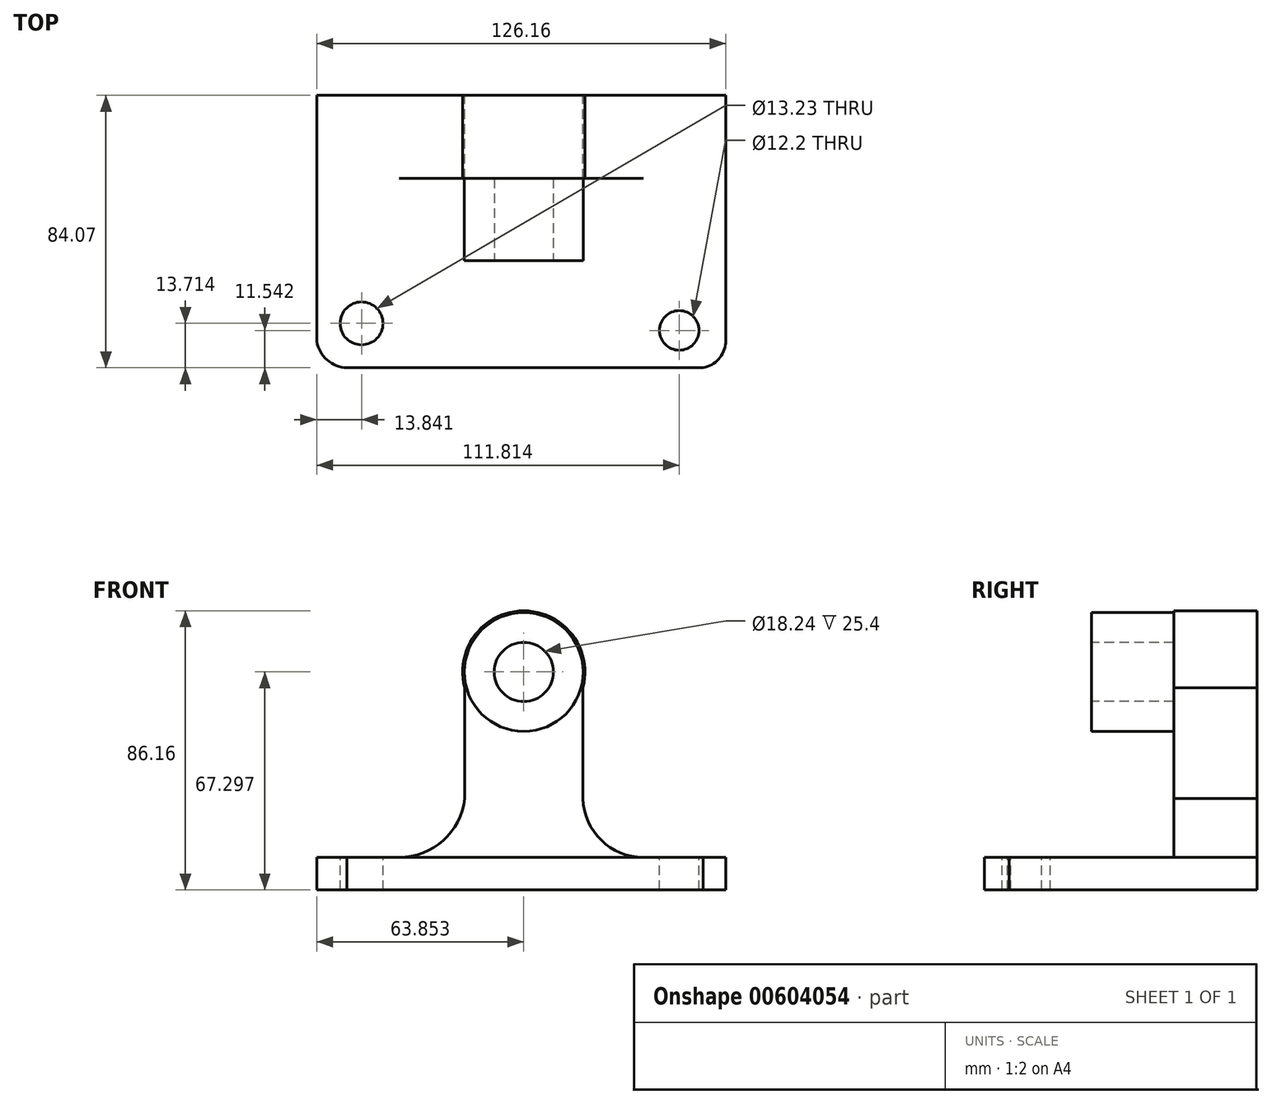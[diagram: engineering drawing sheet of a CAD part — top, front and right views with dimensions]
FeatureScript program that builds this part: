
annotation { "Feature Type Name" : "Feature", "Feature Type Description" : "" }
export const myFeature = defineFeature(function(context is Context, id is Id, definition is map)
    precondition{}
    {
        {
            var Q0;
            Q0=qCreatedBy(makeId("Front.planeOp"),FACE);
            var sketch = newSketch(context, id + "F0", { "sketchPlane" : qUnion([Q0])});
            skLineSegment(sketch, "E0.bottom", {"start": v(-69.62, 0) * mm, "end": v(5.74, 0) * mm});
            skLineSegment(sketch, "E0.top", {"start": v(-69.62, 76.13) * mm, "end": v(5.74, 76.13) * mm});
            skLineSegment(sketch, "E0.left", {"start": v(-69.62, 0) * mm, "end": v(-69.62, 76.13) * mm});
            skLineSegment(sketch, "E0.right", {"start": v(5.74, 0) * mm, "end": v(5.74, 76.13) * mm});
            skSolve(sketch);
        }
        {
            var Q0;
            Q0=makeQuery(id+"F0.imprint","IMPRINT",FACE,{"disambiguationData":[TD([[makeQuery(id+"F0.imprint","IMPRINT",EDGE,{"derivedFrom":sQuery(id+"F0.wireOp",EDGE,"E0.bottom")}),1.0]])]});
            extrude(context, id + "F1", {"entities" : qUnion([Q0]), "depth" : 25.4 * mm, "offsetDistance" : 25.4 * mm});
        }
        {
            var Q0;
            Q0=makeQuery(id+"F1.opExtrude","CAP_FACE",FACE,{"disambiguationData":[OSD([sQuery(id+"F0.wireOp",EDGE,"E0.bottom"),sQuery(id+"F0.wireOp",EDGE,"E0.top"),sQuery(id+"F0.wireOp",EDGE,"E0.left"),sQuery(id+"F0.wireOp",EDGE,"E0.right")])],"isStart":true});
            extrude(context, id + "F2", {"entities" : qUnion([Q0]), "operationType" : NewBodyOperationType.ADD, "depth" : 25.4 * mm, "offsetDistance" : 25.4 * mm});
        }
        {
            var Q0;
            Q0=makeQuery(id+"F2.opExtrude","CAP_FACE",FACE,{"disambiguationData":[OSD([sQuery(id+"F0.wireOp",EDGE,"E0.bottom"),sQuery(id+"F0.wireOp",EDGE,"E0.top"),sQuery(id+"F0.wireOp",EDGE,"E0.left"),sQuery(id+"F0.wireOp",EDGE,"E0.right")])],"isStart":false});
            extrude(context, id + "F3", {"entities" : qUnion([Q0]), "operationType" : NewBodyOperationType.ADD, "depth" : 25.65 * mm, "offsetDistance" : 25.4 * mm});
        }
        {
            var Q0;
            Q0=makeQuery(id+"F3.opExtrude","CAP_FACE",FACE,{"disambiguationData":[OSD([sQuery(id+"F0.wireOp",EDGE,"E0.bottom"),sQuery(id+"F0.wireOp",EDGE,"E0.top"),sQuery(id+"F0.wireOp",EDGE,"E0.left"),sQuery(id+"F0.wireOp",EDGE,"E0.right")])],"isStart":false});
            var sketch = newSketch(context, id + "F4", { "sketchPlane" : qUnion([Q0])});
            skCircle(sketch, "E1", {"center": v(31.17, 57.22) * mm, "radius": 18.86 * mm});
            skSolve(sketch);
        }
        {
            var Q0;
            Q0=makeQuery(id+"F4.imprint","IMPRINT",FACE,{"disambiguationData":[TD([[makeQuery(id+"F4.imprint","IMPRINT",EDGE,{"derivedFrom":sQuery(id+"F4.wireOp",EDGE,"E1")}),-1.0]])]});
            extrude(context, id + "F5", {"entities" : qUnion([Q0]), "operationType" : NewBodyOperationType.REMOVE, "oppositeDirection" : true, "depth" : 25.4 * mm, "offsetDistance" : 25.4 * mm});
        }
        {
            var Q0;
            Q0=makeQuery(id+"F5.boolean.opBoolean","COPY",FACE,{"derivedFrom":makeQuery(id+"F5.opExtrude","CAP_FACE",FACE,{"disambiguationData":[OSD([sQuery(id+"F0.wireOp",EDGE,"E0.bottom"),sQuery(id+"F0.wireOp",EDGE,"E0.top"),sQuery(id+"F0.wireOp",EDGE,"E0.left"),sQuery(id+"F0.wireOp",EDGE,"E0.right"),sQuery(id+"F4.wireOp",EDGE,"E1")])],"isStart":false})});
            var sketch = newSketch(context, id + "F6", { "sketchPlane" : qUnion([Q0])});
            skLineSegment(sketch, "E2", {"start": v(12.94, 62.06) * mm, "end": v(12.94, 18.14) * mm});
            skLineSegment(sketch, "E3", {"start": v(49.4, 62.06) * mm, "end": v(49.4, 18.14) * mm});
            skArc(sketch, "E4", {"start": v(-5.74, 0) * mm, "mid": v(7.28, 5.28) * mm, "end": v(12.94, 18.14) * mm});
            skArc(sketch, "E5", {"start": v(49.4, 18.14) * mm, "mid": v(56.04, 5.2) * mm, "end": v(69.62, 0) * mm});
            skSolve(sketch);
        }
        {
            var Q0;
            {var subQ1=sQuery(id+"F6.wireOp",EDGE,"E4");Q0=makeQuery(id+"F6.imprint","IMPRINT",FACE,{"disambiguationData":[TD([[makeQuery(id+"F6.imprint","IMPRINT",EDGE,{"derivedFrom":subQ1}),1.0]])]});}
            extrude(context, id + "F7", {"entities" : qUnion([Q0]), "operationType" : NewBodyOperationType.REMOVE, "oppositeDirection" : true, "depth" : 25.4 * mm, "offsetDistance" : 25.4 * mm});
        }
        {
            var Q0;
            Q0=makeQuery(id+"F7.boolean.opBoolean","COPY",FACE,{"derivedFrom":makeQuery(id+"F7.opExtrude","CAP_FACE",FACE,{"disambiguationData":[OSD([sQuery(id+"F0.wireOp",EDGE,"E0.top"),sQuery(id+"F0.wireOp",EDGE,"E0.left"),sQuery(id+"F0.wireOp",EDGE,"E0.right"),sQuery(id+"F4.wireOp",EDGE,"E1"),sQuery(id+"F6.wireOp",EDGE,"E2"),sQuery(id+"F6.wireOp",EDGE,"E3"),sQuery(id+"F6.wireOp",EDGE,"E4"),sQuery(id+"F6.wireOp",EDGE,"E5")])],"isStart":false})});
            var sketch = newSketch(context, id + "F8", { "sketchPlane" : qUnion([Q0])});
            skLineSegment(sketch, "E6.bottom", {"start": v(-5.74, 0) * mm, "end": v(69.93, 0) * mm});
            skLineSegment(sketch, "E6.top", {"start": v(-5.74, -10.08) * mm, "end": v(69.93, -10.08) * mm});
            skLineSegment(sketch, "E6.left", {"start": v(-5.74, 0) * mm, "end": v(-5.74, -10.08) * mm});
            skLineSegment(sketch, "E6.right", {"start": v(69.93, 0) * mm, "end": v(69.93, -10.08) * mm});
            skSolve(sketch);
        }
        {
            var Q0;
            Q0=makeQuery(id+"F8.imprint","IMPRINT",FACE,{"disambiguationData":[TD([[makeQuery(id+"F8.imprint","IMPRINT",EDGE,{"derivedFrom":sQuery(id+"F8.wireOp",EDGE,"E6.top")}),1.0]])]});
            extrude(context, id + "F9", {"entities" : qUnion([Q0]), "operationType" : NewBodyOperationType.ADD, "depth" : 25.4 * mm, "offsetDistance" : 25.4 * mm});
        }
        {
            var Q0;
            Q0=makeQuery(id+"F9.opExtrude","CAP_FACE",FACE,{"disambiguationData":[OSD([sQuery(id+"F8.wireOp",EDGE,"E6.bottom"),sQuery(id+"F8.wireOp",EDGE,"E6.top"),sQuery(id+"F8.wireOp",EDGE,"E6.left"),sQuery(id+"F8.wireOp",EDGE,"E6.right")])],"isStart":true});
            extrude(context, id + "F10", {"entities" : qUnion([Q0]), "operationType" : NewBodyOperationType.ADD, "depth" : 25.4 * mm, "offsetDistance" : 25.4 * mm});
        }
        {
            var Q0;
            Q0=makeQuery(id+"F7.boolean.opBoolean","COPY",FACE,{"derivedFrom":makeQuery(id+"F7.opExtrude","CAP_FACE",FACE,{"disambiguationData":[OSD([sQuery(id+"F0.wireOp",EDGE,"E0.top"),sQuery(id+"F0.wireOp",EDGE,"E0.left"),sQuery(id+"F0.wireOp",EDGE,"E0.right"),sQuery(id+"F4.wireOp",EDGE,"E1"),sQuery(id+"F6.wireOp",EDGE,"E2"),sQuery(id+"F6.wireOp",EDGE,"E3"),sQuery(id+"F6.wireOp",EDGE,"E4"),sQuery(id+"F6.wireOp",EDGE,"E5")])],"isStart":false})});
            extrude(context, id + "F11", {"entities" : qUnion([Q0]), "operationType" : NewBodyOperationType.REMOVE, "oppositeDirection" : true, "depth" : 25.4 * mm, "offsetDistance" : 25.4 * mm});
        }
        {
            var Q0;
            Q0=makeQuery(id+"F11.boolean.opBoolean","COPY",FACE,{"derivedFrom":makeQuery(id+"F11.opExtrude","CAP_FACE",FACE,{"disambiguationData":[OSD([sQuery(id+"F0.wireOp",EDGE,"E0.top"),sQuery(id+"F0.wireOp",EDGE,"E0.left"),sQuery(id+"F0.wireOp",EDGE,"E0.right"),sQuery(id+"F4.wireOp",EDGE,"E1"),sQuery(id+"F6.wireOp",EDGE,"E2"),sQuery(id+"F6.wireOp",EDGE,"E3"),sQuery(id+"F6.wireOp",EDGE,"E4"),sQuery(id+"F6.wireOp",EDGE,"E5")])],"isStart":false})});
            extrude(context, id + "F12", {"entities" : qUnion([Q0]), "operationType" : NewBodyOperationType.REMOVE, "oppositeDirection" : true, "depth" : 25.4 * mm, "offsetDistance" : 25.4 * mm});
        }
        {
            var Q0;
            {var subQ0=sQuery(id+"F8.wireOp",EDGE,"E6.top");var subQ4=sQuery(id+"F0.wireOp",EDGE,"E0.right");var subQ7=makeQuery(id+"F1.opExtrude","SWEPT_FACE",FACE,{"disambiguationData":[OSD([subQ4])]});var subQ8=makeQuery(id+"F3.opExtrude","SWEPT_FACE",FACE,{"disambiguationData":[OSD([subQ4])]});var subQ10=sQuery(id+"F8.wireOp",EDGE,"E6.left");var subQ12=makeQuery(id+"F2.opExtrude","SWEPT_FACE",FACE,{"disambiguationData":[OSD([subQ4])]});var subQ13=makeQuery(id+"F9.opExtrude","SWEPT_FACE",FACE,{"disambiguationData":[OSD([subQ10])]});var subQ14=makeQuery(id+"F10.opExtrude","SWEPT_FACE",FACE,{"disambiguationData":[OSD([subQ10])]});Q0=makeQuery(id+"F11.boolean.opBoolean","SPLIT",FACE,{"disambiguationData":[TD([makeQuery(id+"F9.opExtrude","SWEPT_FACE",FACE,{"disambiguationData":[OSD([subQ0])]})])],"derivedFrom":makeQuery(id+"F10.boolean.opBoolean","MERGE",FACE,{"derivedFrom":[makeQuery(id+"F3.boolean.opBoolean","MERGE",FACE,{"derivedFrom":[makeQuery(id+"F2.boolean.opBoolean","MERGE",FACE,{"derivedFrom":[subQ7,subQ12]}),subQ8]}),subQ13,subQ14]})});}
            extrude(context, id + "F13", {"entities" : qUnion([Q0]), "operationType" : NewBodyOperationType.ADD, "depth" : 25.4 * mm, "offsetDistance" : 25.4 * mm});
        }
        {
            var Q0;
            {var subQ0=sQuery(id+"F8.wireOp",EDGE,"E6.right");Q0=makeQuery(id+"F10.boolean.opBoolean","MERGE",FACE,{"derivedFrom":[makeQuery(id+"F9.opExtrude","SWEPT_FACE",FACE,{"disambiguationData":[OSD([subQ0])]}),makeQuery(id+"F10.opExtrude","SWEPT_FACE",FACE,{"disambiguationData":[OSD([subQ0])]})]});}
            extrude(context, id + "F14", {"entities" : qUnion([Q0]), "operationType" : NewBodyOperationType.ADD, "depth" : 25.4 * mm, "offsetDistance" : 25.4 * mm});
        }
        {
            var Q0;
            {var subQ0=sQuery(id+"F8.wireOp",EDGE,"E6.right");var subQ1=sQuery(id+"F8.wireOp",EDGE,"E6.left");Q0=makeQuery(id+"F14.boolean.opBoolean","MERGE",FACE,{"derivedFrom":[makeQuery(id+"F13.boolean.opBoolean","MERGE",FACE,{"derivedFrom":[makeQuery(id+"F9.boolean.opBoolean","MERGE",FACE,{"derivedFrom":[makeQuery(id+"F5.boolean.opBoolean","COPY",FACE,{"derivedFrom":makeQuery(id+"F5.opExtrude","CAP_FACE",FACE,{"disambiguationData":[OSD([sQuery(id+"F0.wireOp",EDGE,"E0.bottom"),sQuery(id+"F0.wireOp",EDGE,"E0.top"),sQuery(id+"F0.wireOp",EDGE,"E0.left"),sQuery(id+"F0.wireOp",EDGE,"E0.right"),sQuery(id+"F4.wireOp",EDGE,"E1")])],"isStart":false})}),makeQuery(id+"F9.opExtrude","CAP_FACE",FACE,{"disambiguationData":[OSD([sQuery(id+"F8.wireOp",EDGE,"E6.bottom"),sQuery(id+"F8.wireOp",EDGE,"E6.top"),subQ1,subQ0])],"isStart":false})]}),makeQuery(id+"F13.opExtrude","SWEPT_FACE",FACE,{"disambiguationData":[OSD([subQ1]),TDD([makeQuery(id+"F9.opExtrude","CAP_EDGE",EDGE,{"disambiguationData":[OSD([subQ1])],"isStart":false})])]})]}),makeQuery(id+"F14.opExtrude","SWEPT_FACE",FACE,{"disambiguationData":[OSD([subQ0]),TDD([makeQuery(id+"F9.opExtrude","CAP_EDGE",EDGE,{"disambiguationData":[OSD([subQ0])],"isStart":false})])]})]});}
            extrude(context, id + "F15", {"entities" : qUnion([Q0]), "operationType" : NewBodyOperationType.ADD, "depth" : 25.4 * mm, "offsetDistance" : 25.4 * mm});
        }
        {
            var Q0;
            {var subQ0=sQuery(id+"F0.wireOp",EDGE,"E0.right");var subQ1=sQuery(id+"F0.wireOp",EDGE,"E0.left");var subQ2=sQuery(id+"F0.wireOp",EDGE,"E0.top");var subQ3=sQuery(id+"F0.wireOp",EDGE,"E0.bottom");Q0=makeQuery(id+"F15.boolean.opBoolean","MERGE",FACE,{"derivedFrom":[makeQuery(id+"F3.opExtrude","CAP_FACE",FACE,{"disambiguationData":[OSD([subQ3,subQ2,subQ1,subQ0])],"isStart":false}),makeQuery(id+"F15.opExtrude","CAP_FACE",FACE,{"disambiguationData":[OSD([subQ3,subQ2,subQ1,subQ0,sQuery(id+"F4.wireOp",EDGE,"E1"),sQuery(id+"F8.wireOp",EDGE,"E6.bottom"),sQuery(id+"F8.wireOp",EDGE,"E6.top"),sQuery(id+"F8.wireOp",EDGE,"E6.left"),sQuery(id+"F8.wireOp",EDGE,"E6.right")])],"isStart":false})]});}
            extrude(context, id + "F16", {"entities" : qUnion([Q0]), "operationType" : NewBodyOperationType.REMOVE, "oppositeDirection" : true, "depth" : 25.4 * mm, "offsetDistance" : 25.4 * mm});
        }
        {
            var Q0;
            Q0=makeQuery(id+"F16.boolean.opBoolean","COPY",FACE,{"derivedFrom":makeQuery(id+"F16.opExtrude","CAP_FACE",FACE,{"disambiguationData":[OSD([sQuery(id+"F0.wireOp",EDGE,"E0.bottom"),sQuery(id+"F0.wireOp",EDGE,"E0.top"),sQuery(id+"F0.wireOp",EDGE,"E0.left"),sQuery(id+"F0.wireOp",EDGE,"E0.right"),sQuery(id+"F4.wireOp",EDGE,"E1"),sQuery(id+"F8.wireOp",EDGE,"E6.bottom"),sQuery(id+"F8.wireOp",EDGE,"E6.top"),sQuery(id+"F8.wireOp",EDGE,"E6.left"),sQuery(id+"F8.wireOp",EDGE,"E6.right")])],"isStart":false})});
            var sketch = newSketch(context, id + "F17", { "sketchPlane" : qUnion([Q0])});
            skCircle(sketch, "E7", {"center": v(31.17, 57.22) * mm, "radius": 18.64 * mm});
            skSolve(sketch);
        }
        {
            var Q0;
            Q0=makeQuery(id+"F17.imprint","IMPRINT",FACE,{"disambiguationData":[TD([[makeQuery(id+"F17.imprint","IMPRINT",EDGE,{"derivedFrom":sQuery(id+"F17.wireOp",EDGE,"E7")}),1.0]])]});
            extrude(context, id + "F18", {"entities" : qUnion([Q0]), "operationType" : NewBodyOperationType.REMOVE, "depth" : 25.4 * mm, "offsetDistance" : 25.4 * mm});
        }
        {
            var Q0;
            Q0=makeQuery(id+"F1.opExtrude","CAP_FACE",FACE,{"disambiguationData":[OSD([sQuery(id+"F0.wireOp",EDGE,"E0.bottom"),sQuery(id+"F0.wireOp",EDGE,"E0.top"),sQuery(id+"F0.wireOp",EDGE,"E0.left"),sQuery(id+"F0.wireOp",EDGE,"E0.right")])],"isStart":false});
            var sketch = newSketch(context, id + "F19", { "sketchPlane" : qUnion([Q0])});
            skCircle(sketch, "E8", {"center": v(-31.17, 57.22) * mm, "radius": 18.34 * mm});
            skSolve(sketch);
        }
        {
            var Q0;
            Q0=makeQuery(id+"F19.imprint","IMPRINT",FACE,{"disambiguationData":[TD([[makeQuery(id+"F19.imprint","IMPRINT",EDGE,{"derivedFrom":sQuery(id+"F19.wireOp",EDGE,"E8")}),1.0]])]});
            extrude(context, id + "F20", {"entities" : qUnion([Q0]), "operationType" : NewBodyOperationType.ADD, "depth" : 25.4 * mm, "offsetDistance" : 25.4 * mm});
        }
        {
            var Q0;
            Q0=makeQuery(id+"F16.boolean.opBoolean","COPY",FACE,{"derivedFrom":makeQuery(id+"F16.opExtrude","CAP_FACE",FACE,{"disambiguationData":[OSD([sQuery(id+"F0.wireOp",EDGE,"E0.bottom"),sQuery(id+"F0.wireOp",EDGE,"E0.top"),sQuery(id+"F0.wireOp",EDGE,"E0.left"),sQuery(id+"F0.wireOp",EDGE,"E0.right"),sQuery(id+"F4.wireOp",EDGE,"E1"),sQuery(id+"F8.wireOp",EDGE,"E6.bottom"),sQuery(id+"F8.wireOp",EDGE,"E6.top"),sQuery(id+"F8.wireOp",EDGE,"E6.left"),sQuery(id+"F8.wireOp",EDGE,"E6.right")])],"isStart":false})});
            extrude(context, id + "F21", {"entities" : qUnion([Q0]), "operationType" : NewBodyOperationType.REMOVE, "oppositeDirection" : true, "depth" : 25.4 * mm, "offsetDistance" : 25.4 * mm});
        }
        {
            var Q0;
            {var subQ0=sQuery(id+"F8.wireOp",EDGE,"E6.right");var subQ1=sQuery(id+"F8.wireOp",EDGE,"E6.left");Q0=makeQuery(id+"F14.boolean.opBoolean","MERGE",FACE,{"derivedFrom":[makeQuery(id+"F13.boolean.opBoolean","MERGE",FACE,{"derivedFrom":[makeQuery(id+"F10.opExtrude","CAP_FACE",FACE,{"disambiguationData":[OSD([sQuery(id+"F8.wireOp",EDGE,"E6.bottom"),sQuery(id+"F8.wireOp",EDGE,"E6.top"),subQ1,subQ0])],"isStart":false}),makeQuery(id+"F13.opExtrude","SWEPT_FACE",FACE,{"disambiguationData":[OSD([subQ1]),TDD([makeQuery(id+"F10.opExtrude","CAP_EDGE",EDGE,{"disambiguationData":[OSD([subQ1])],"isStart":false})])]})]}),makeQuery(id+"F14.opExtrude","SWEPT_FACE",FACE,{"disambiguationData":[OSD([subQ0]),TDD([makeQuery(id+"F10.opExtrude","CAP_EDGE",EDGE,{"disambiguationData":[OSD([subQ0])],"isStart":false})])]})]});}
            extrude(context, id + "F22", {"entities" : qUnion([Q0]), "operationType" : NewBodyOperationType.ADD, "depth" : 58.67 * mm, "offsetDistance" : 25.4 * mm});
        }
        {
            var Q0;
            {var subQ0=sQuery(id+"F8.wireOp",EDGE,"E6.right");var subQ1=sQuery(id+"F8.wireOp",EDGE,"E6.left");var subQ2=sQuery(id+"F8.wireOp",EDGE,"E6.bottom");var subQ3=sQuery(id+"F6.wireOp",EDGE,"E4");var subQ4=sQuery(id+"F0.wireOp",EDGE,"E0.right");var subQ5=sQuery(id+"F0.wireOp",EDGE,"E0.bottom");Q0=makeQuery(id+"F22.boolean.opBoolean","MERGE",FACE,{"derivedFrom":[makeQuery(id+"F15.boolean.opBoolean","MERGE",FACE,{"derivedFrom":[makeQuery(id+"F13.opExtrude","SWEPT_FACE",FACE,{"disambiguationData":[OSD([subQ5,subQ4,subQ3,subQ2,subQ1])]}),makeQuery(id+"F15.opExtrude","SWEPT_FACE",FACE,{"disambiguationData":[OSD([subQ5,subQ4,subQ3,subQ2,subQ1])]})]}),makeQuery(id+"F15.boolean.opBoolean","MERGE",FACE,{"derivedFrom":[makeQuery(id+"F14.boolean.opBoolean","MERGE",FACE,{"derivedFrom":[makeQuery(id+"F10.boolean.opBoolean","MERGE",FACE,{"derivedFrom":[makeQuery(id+"F9.opExtrude","SWEPT_FACE",FACE,{"disambiguationData":[OSD([subQ2])]}),makeQuery(id+"F10.opExtrude","SWEPT_FACE",FACE,{"disambiguationData":[OSD([subQ2])]})]}),makeQuery(id+"F14.opExtrude","SWEPT_FACE",FACE,{"disambiguationData":[OSD([subQ2,subQ0])]})]}),makeQuery(id+"F15.opExtrude","SWEPT_FACE",FACE,{"disambiguationData":[OSD([subQ2,subQ0])]})]}),makeQuery(id+"F22.opExtrude","SWEPT_FACE",FACE,{"disambiguationData":[OSD([subQ5,subQ4,subQ3,subQ2,subQ1,subQ0])]})]});}
            var sketch = newSketch(context, id + "F23", { "sketchPlane" : qUnion([Q0])});
            skLineSegment(sketch, "E9", {"start": v(-69.62, -25.4) * mm, "end": v(-69.62, -83.82) * mm});
            skLineSegment(sketch, "E10", {"start": v(5.74, -25.4) * mm, "end": v(5.74, -83.82) * mm});
            skSolve(sketch);
        }
        {
            var Q0;
            {var subQ12=sQuery(id+"F23.wireOp",EDGE,"E9");Q0=makeQuery(id+"F23.imprint","IMPRINT",FACE,{"disambiguationData":[TD([[makeQuery(id+"F23.imprint","IMPRINT",EDGE,{"derivedFrom":subQ12}),-1.0]])]});}
            extrude(context, id + "F24", {"entities" : qUnion([Q0]), "operationType" : NewBodyOperationType.REMOVE, "oppositeDirection" : true, "depth" : 25.4 * mm, "offsetDistance" : 25.4 * mm});
        }
        {
            var Q0;
            {var subQ0=sQuery(id+"F8.wireOp",EDGE,"E6.right");var subQ1=sQuery(id+"F8.wireOp",EDGE,"E6.left");var subQ2=sQuery(id+"F8.wireOp",EDGE,"E6.bottom");var subQ3=sQuery(id+"F6.wireOp",EDGE,"E4");var subQ4=sQuery(id+"F0.wireOp",EDGE,"E0.right");var subQ5=sQuery(id+"F0.wireOp",EDGE,"E0.bottom");Q0=makeQuery(id+"F22.boolean.opBoolean","MERGE",FACE,{"derivedFrom":[makeQuery(id+"F15.boolean.opBoolean","MERGE",FACE,{"derivedFrom":[makeQuery(id+"F13.opExtrude","SWEPT_FACE",FACE,{"disambiguationData":[OSD([subQ5,subQ4,subQ3,subQ2,subQ1])]}),makeQuery(id+"F15.opExtrude","SWEPT_FACE",FACE,{"disambiguationData":[OSD([subQ5,subQ4,subQ3,subQ2,subQ1])]})]}),makeQuery(id+"F15.boolean.opBoolean","MERGE",FACE,{"derivedFrom":[makeQuery(id+"F14.boolean.opBoolean","MERGE",FACE,{"derivedFrom":[makeQuery(id+"F10.boolean.opBoolean","MERGE",FACE,{"derivedFrom":[makeQuery(id+"F9.opExtrude","SWEPT_FACE",FACE,{"disambiguationData":[OSD([subQ2])]}),makeQuery(id+"F10.opExtrude","SWEPT_FACE",FACE,{"disambiguationData":[OSD([subQ2])]})]}),makeQuery(id+"F14.opExtrude","SWEPT_FACE",FACE,{"disambiguationData":[OSD([subQ2,subQ0])]})]}),makeQuery(id+"F15.opExtrude","SWEPT_FACE",FACE,{"disambiguationData":[OSD([subQ2,subQ0])]})]}),makeQuery(id+"F22.opExtrude","SWEPT_FACE",FACE,{"disambiguationData":[OSD([subQ5,subQ4,subQ3,subQ2,subQ1,subQ0])]})]});}
            var sketch = newSketch(context, id + "F25", { "sketchPlane" : qUnion([Q0])});
            skLineSegment(sketch, "E11", {"start": v(5.74, -25.4) * mm, "end": v(5.74, -83.82) * mm});
            skSolve(sketch);
        }
        {
            var Q0;
            {var subQ8=sQuery(id+"F25.wireOp",EDGE,"E11");Q0=makeQuery(id+"F25.imprint","IMPRINT",FACE,{"disambiguationData":[TD([[makeQuery(id+"F25.imprint","IMPRINT",EDGE,{"derivedFrom":subQ8}),1.0]])]});}
            extrude(context, id + "F26", {"entities" : qUnion([Q0]), "operationType" : NewBodyOperationType.REMOVE, "oppositeDirection" : true, "depth" : 25.4 * mm, "offsetDistance" : 25.4 * mm});
        }
        {
            var Q0;
            Q0=makeQuery(id+"F24.boolean.opBoolean","COPY",FACE,{"derivedFrom":makeQuery(id+"F24.opExtrude","SWEPT_FACE",FACE,{"disambiguationData":[OSD([sQuery(id+"F0.wireOp",EDGE,"E0.bottom"),sQuery(id+"F0.wireOp",EDGE,"E0.left"),sQuery(id+"F6.wireOp",EDGE,"E5"),sQuery(id+"F8.wireOp",EDGE,"E6.bottom"),sQuery(id+"F8.wireOp",EDGE,"E6.top"),sQuery(id+"F8.wireOp",EDGE,"E6.left"),sQuery(id+"F8.wireOp",EDGE,"E6.right"),sQuery(id+"F23.wireOp",EDGE,"E9")])]})});
            extrude(context, id + "F27", {"entities" : qUnion([Q0]), "operationType" : NewBodyOperationType.ADD, "depth" : 25.4 * mm, "offsetDistance" : 25.4 * mm});
        }
        {
            var Q0;
            Q0=makeQuery(id+"F26.boolean.opBoolean","COPY",FACE,{"derivedFrom":makeQuery(id+"F26.opExtrude","SWEPT_FACE",FACE,{"disambiguationData":[OSD([sQuery(id+"F0.wireOp",EDGE,"E0.bottom"),sQuery(id+"F0.wireOp",EDGE,"E0.right"),sQuery(id+"F6.wireOp",EDGE,"E4"),sQuery(id+"F8.wireOp",EDGE,"E6.bottom"),sQuery(id+"F8.wireOp",EDGE,"E6.left"),sQuery(id+"F25.wireOp",EDGE,"E11")])]})});
            extrude(context, id + "F28", {"entities" : qUnion([Q0]), "operationType" : NewBodyOperationType.ADD, "depth" : 25.4 * mm, "offsetDistance" : 25.4 * mm});
        }
        {
            var Q0;
            {var subQ0=sQuery(id+"F8.wireOp",EDGE,"E6.left");var subQ1=sQuery(id+"F8.wireOp",EDGE,"E6.bottom");var subQ2=sQuery(id+"F6.wireOp",EDGE,"E4");var subQ3=sQuery(id+"F0.wireOp",EDGE,"E0.right");var subQ4=sQuery(id+"F0.wireOp",EDGE,"E0.bottom");var subQ5=sQuery(id+"F23.wireOp",EDGE,"E9");var subQ6=sQuery(id+"F8.wireOp",EDGE,"E6.right");var subQ7=sQuery(id+"F8.wireOp",EDGE,"E6.top");var subQ8=sQuery(id+"F6.wireOp",EDGE,"E5");var subQ9=sQuery(id+"F0.wireOp",EDGE,"E0.left");var subQ10=makeQuery(id+"F24.opExtrude","CAP_EDGE",EDGE,{"disambiguationData":[OSD([subQ4,subQ9,subQ8,subQ1,subQ7,subQ0,subQ6,subQ5])],"isStart":true});var subQ11=makeQuery(id+"F9.opExtrude","SWEPT_FACE",FACE,{"disambiguationData":[OSD([subQ1])]});var subQ15=makeQuery(id+"F10.opExtrude","SWEPT_FACE",FACE,{"disambiguationData":[OSD([subQ1])]});var subQ16=makeQuery(id+"F3.boolean.opBoolean","MERGE",EDGE,{"derivedFrom":[makeQuery(id+"F2.boolean.opBoolean","MERGE",EDGE,{"derivedFrom":[makeQuery(id+"F1.opExtrude","SWEPT_EDGE",EDGE,{"disambiguationData":[OSD([subQ4,subQ9])]}),makeQuery(id+"F2.opExtrude","SWEPT_EDGE",EDGE,{"disambiguationData":[OSD([subQ4,subQ9])]})]}),makeQuery(id+"F3.opExtrude","SWEPT_EDGE",EDGE,{"disambiguationData":[OSD([subQ4,subQ9])]})]});var subQ17=makeQuery(id+"F7.boolean.opBoolean","SPLIT",EDGE,{"derivedFrom":subQ16});Q0=makeQuery(id+"F28.boolean.opBoolean","MERGE",FACE,{"derivedFrom":[makeQuery(id+"F27.boolean.opBoolean","MERGE",FACE,{"derivedFrom":[makeQuery(id+"F22.boolean.opBoolean","MERGE",FACE,{"derivedFrom":[makeQuery(id+"F15.boolean.opBoolean","MERGE",FACE,{"derivedFrom":[makeQuery(id+"F13.opExtrude","SWEPT_FACE",FACE,{"disambiguationData":[OSD([subQ4,subQ3,subQ2,subQ1,subQ0])]}),makeQuery(id+"F15.opExtrude","SWEPT_FACE",FACE,{"disambiguationData":[OSD([subQ4,subQ3,subQ2,subQ1,subQ0])]})]}),makeQuery(id+"F15.boolean.opBoolean","MERGE",FACE,{"derivedFrom":[makeQuery(id+"F14.boolean.opBoolean","MERGE",FACE,{"derivedFrom":[makeQuery(id+"F10.boolean.opBoolean","MERGE",FACE,{"derivedFrom":[subQ11,subQ15]}),makeQuery(id+"F14.opExtrude","SWEPT_FACE",FACE,{"disambiguationData":[OSD([subQ1,subQ6])]})]}),makeQuery(id+"F15.opExtrude","SWEPT_FACE",FACE,{"disambiguationData":[OSD([subQ1,subQ6])]})]}),makeQuery(id+"F22.opExtrude","SWEPT_FACE",FACE,{"disambiguationData":[OSD([subQ4,subQ3,subQ2,subQ1,subQ0,subQ6])]})]}),makeQuery(id+"F27.opExtrude","SWEPT_FACE",FACE,{"disambiguationData":[OSD([subQ4,subQ9,subQ8,subQ1,subQ7,subQ0,subQ6,subQ5]),TDD([makeQuery(id+"F24.boolean.opBoolean","MERGE",EDGE,{"derivedFrom":[makeQuery(id+"F22.boolean.opBoolean","MERGE",EDGE,{"derivedFrom":[makeQuery(id+"F12.boolean.opBoolean","MERGE",EDGE,{"derivedFrom":[makeQuery(id+"F10.boolean.opBoolean","SPLIT",EDGE,{"disambiguationData":[topologyDisambiguationEdgeConnected([makeQuery(id+"F1.opExtrude","SWEPT_FACE",FACE,{"disambiguationData":[OSD([subQ4])]})])],"derivedFrom":subQ17}),makeQuery(id+"F12.opExtrude","SWEPT_EDGE",EDGE,{"disambiguationData":[OSD([subQ4,subQ9,subQ8,subQ1,subQ7,subQ0,subQ6])]})]}),makeQuery(id+"F15.boolean.opBoolean","MERGE",EDGE,{"derivedFrom":[makeQuery(id+"F11.boolean.opBoolean","MERGE",EDGE,{"derivedFrom":[makeQuery(id+"F7.boolean.opBoolean","MERGE",EDGE,{"derivedFrom":[subQ16,makeQuery(id+"F7.opExtrude","SWEPT_EDGE",EDGE,{"disambiguationData":[OSD([subQ4,subQ9,subQ8])]})]}),makeQuery(id+"F10.boolean.opBoolean","SPLIT",EDGE,{"disambiguationData":[topologyDisambiguationEdgeConnected([subQ11])],"derivedFrom":subQ17}),makeQuery(id+"F11.opExtrude","SWEPT_EDGE",EDGE,{"disambiguationData":[OSD([subQ4,subQ9,subQ8])]})]}),makeQuery(id+"F15.opExtrude","SWEPT_EDGE",EDGE,{"disambiguationData":[OSD([subQ4,subQ9,subQ8])]})]})]}),subQ10]}),makeQuery(id+"F24.boolean.opBoolean","COPY",EDGE,{"derivedFrom":subQ10})])]})]}),makeQuery(id+"F28.opExtrude","SWEPT_FACE",FACE,{"disambiguationData":[OSD([subQ4,subQ3,subQ2,subQ1,subQ0,sQuery(id+"F25.wireOp",EDGE,"E11")])]})]});}
            var sketch = newSketch(context, id + "F29", { "sketchPlane" : qUnion([Q0])});
            skArc(sketch, "E12", {"start": v(-95.02, -70.09) * mm, "mid": v(-91.62, -79.2) * mm, "end": v(-83.06, -83.82) * mm});
            skArc(sketch, "E13", {"start": v(19.9, -83.82) * mm, "mid": v(28.54, -79.13) * mm, "end": v(31.14, -69.65) * mm});
            skCircle(sketch, "E14", {"center": v(-81.18, -70.1) * mm, "radius": 6.61 * mm});
            skCircle(sketch, "E15", {"center": v(18.72, -71.35) * mm, "radius": 6.6 * mm});
            skSolve(sketch);
        }
        {
            var Q0;
            Q0=makeQuery(id+"F29.imprint","IMPRINT",FACE,{"disambiguationData":[TD([[makeQuery(id+"F29.imprint","IMPRINT",EDGE,{"derivedFrom":sQuery(id+"F29.wireOp",EDGE,"E14")}),1.0]])]});
            extrude(context, id + "F30", {"entities" : qUnion([Q0]), "operationType" : NewBodyOperationType.REMOVE, "oppositeDirection" : true, "depth" : 25.4 * mm, "offsetDistance" : 25.4 * mm});
        }
        {
            var Q0;
            {var subQ0=sQuery(id+"F8.wireOp",EDGE,"E6.left");var subQ1=sQuery(id+"F8.wireOp",EDGE,"E6.bottom");var subQ2=sQuery(id+"F6.wireOp",EDGE,"E4");var subQ3=sQuery(id+"F0.wireOp",EDGE,"E0.right");var subQ4=sQuery(id+"F0.wireOp",EDGE,"E0.bottom");var subQ5=sQuery(id+"F23.wireOp",EDGE,"E9");var subQ6=sQuery(id+"F8.wireOp",EDGE,"E6.right");var subQ7=sQuery(id+"F8.wireOp",EDGE,"E6.top");var subQ8=sQuery(id+"F6.wireOp",EDGE,"E5");var subQ9=sQuery(id+"F0.wireOp",EDGE,"E0.left");var subQ10=makeQuery(id+"F24.opExtrude","CAP_EDGE",EDGE,{"disambiguationData":[OSD([subQ4,subQ9,subQ8,subQ1,subQ7,subQ0,subQ6,subQ5])],"isStart":true});var subQ11=makeQuery(id+"F9.opExtrude","SWEPT_FACE",FACE,{"disambiguationData":[OSD([subQ1])]});var subQ15=makeQuery(id+"F10.opExtrude","SWEPT_FACE",FACE,{"disambiguationData":[OSD([subQ1])]});var subQ16=makeQuery(id+"F3.boolean.opBoolean","MERGE",EDGE,{"derivedFrom":[makeQuery(id+"F2.boolean.opBoolean","MERGE",EDGE,{"derivedFrom":[makeQuery(id+"F1.opExtrude","SWEPT_EDGE",EDGE,{"disambiguationData":[OSD([subQ4,subQ9])]}),makeQuery(id+"F2.opExtrude","SWEPT_EDGE",EDGE,{"disambiguationData":[OSD([subQ4,subQ9])]})]}),makeQuery(id+"F3.opExtrude","SWEPT_EDGE",EDGE,{"disambiguationData":[OSD([subQ4,subQ9])]})]});var subQ17=makeQuery(id+"F7.boolean.opBoolean","SPLIT",EDGE,{"derivedFrom":subQ16});Q0=makeQuery(id+"F28.boolean.opBoolean","MERGE",FACE,{"derivedFrom":[makeQuery(id+"F27.boolean.opBoolean","MERGE",FACE,{"derivedFrom":[makeQuery(id+"F22.boolean.opBoolean","MERGE",FACE,{"derivedFrom":[makeQuery(id+"F15.boolean.opBoolean","MERGE",FACE,{"derivedFrom":[makeQuery(id+"F13.opExtrude","SWEPT_FACE",FACE,{"disambiguationData":[OSD([subQ4,subQ3,subQ2,subQ1,subQ0])]}),makeQuery(id+"F15.opExtrude","SWEPT_FACE",FACE,{"disambiguationData":[OSD([subQ4,subQ3,subQ2,subQ1,subQ0])]})]}),makeQuery(id+"F15.boolean.opBoolean","MERGE",FACE,{"derivedFrom":[makeQuery(id+"F14.boolean.opBoolean","MERGE",FACE,{"derivedFrom":[makeQuery(id+"F10.boolean.opBoolean","MERGE",FACE,{"derivedFrom":[subQ11,subQ15]}),makeQuery(id+"F14.opExtrude","SWEPT_FACE",FACE,{"disambiguationData":[OSD([subQ1,subQ6])]})]}),makeQuery(id+"F15.opExtrude","SWEPT_FACE",FACE,{"disambiguationData":[OSD([subQ1,subQ6])]})]}),makeQuery(id+"F22.opExtrude","SWEPT_FACE",FACE,{"disambiguationData":[OSD([subQ4,subQ3,subQ2,subQ1,subQ0,subQ6])]})]}),makeQuery(id+"F27.opExtrude","SWEPT_FACE",FACE,{"disambiguationData":[OSD([subQ4,subQ9,subQ8,subQ1,subQ7,subQ0,subQ6,subQ5]),TDD([makeQuery(id+"F24.boolean.opBoolean","MERGE",EDGE,{"derivedFrom":[makeQuery(id+"F22.boolean.opBoolean","MERGE",EDGE,{"derivedFrom":[makeQuery(id+"F12.boolean.opBoolean","MERGE",EDGE,{"derivedFrom":[makeQuery(id+"F10.boolean.opBoolean","SPLIT",EDGE,{"disambiguationData":[topologyDisambiguationEdgeConnected([makeQuery(id+"F1.opExtrude","SWEPT_FACE",FACE,{"disambiguationData":[OSD([subQ4])]})])],"derivedFrom":subQ17}),makeQuery(id+"F12.opExtrude","SWEPT_EDGE",EDGE,{"disambiguationData":[OSD([subQ4,subQ9,subQ8,subQ1,subQ7,subQ0,subQ6])]})]}),makeQuery(id+"F15.boolean.opBoolean","MERGE",EDGE,{"derivedFrom":[makeQuery(id+"F11.boolean.opBoolean","MERGE",EDGE,{"derivedFrom":[makeQuery(id+"F7.boolean.opBoolean","MERGE",EDGE,{"derivedFrom":[subQ16,makeQuery(id+"F7.opExtrude","SWEPT_EDGE",EDGE,{"disambiguationData":[OSD([subQ4,subQ9,subQ8])]})]}),makeQuery(id+"F10.boolean.opBoolean","SPLIT",EDGE,{"disambiguationData":[topologyDisambiguationEdgeConnected([subQ11])],"derivedFrom":subQ17}),makeQuery(id+"F11.opExtrude","SWEPT_EDGE",EDGE,{"disambiguationData":[OSD([subQ4,subQ9,subQ8])]})]}),makeQuery(id+"F15.opExtrude","SWEPT_EDGE",EDGE,{"disambiguationData":[OSD([subQ4,subQ9,subQ8])]})]})]}),subQ10]}),makeQuery(id+"F24.boolean.opBoolean","COPY",EDGE,{"derivedFrom":subQ10})])]})]}),makeQuery(id+"F28.opExtrude","SWEPT_FACE",FACE,{"disambiguationData":[OSD([subQ4,subQ3,subQ2,subQ1,subQ0,sQuery(id+"F25.wireOp",EDGE,"E11")])]})]});}
            var sketch = newSketch(context, id + "F31", { "sketchPlane" : qUnion([Q0])});
            skArc(sketch, "E16", {"start": v(-95.02, -72.28) * mm, "mid": v(-92.73, -80.46) * mm, "end": v(-84.92, -83.82) * mm});
            skSolve(sketch);
        }
        {
            var Q0;
            {var subQ0=sQuery(id+"F31.wireOp",EDGE,"E16");var subQ1=sQuery(id+"F23.wireOp",EDGE,"E9");var subQ2=sQuery(id+"F8.wireOp",EDGE,"E6.right");var subQ3=sQuery(id+"F8.wireOp",EDGE,"E6.left");var subQ5=sQuery(id+"F8.wireOp",EDGE,"E6.bottom");var subQ8=sQuery(id+"F0.wireOp",EDGE,"E0.bottom");var subQ17=sQuery(id+"F6.wireOp",EDGE,"E4");var subQ18=sQuery(id+"F0.wireOp",EDGE,"E0.right");var subQ19=makeQuery(id+"F28.boolean.opBoolean","MERGE",EDGE,{"derivedFrom":[makeQuery(id+"F27.boolean.opBoolean","MERGE",EDGE,{"derivedFrom":[makeQuery(id+"F22.opExtrude","CAP_EDGE",EDGE,{"disambiguationData":[OSD([subQ8,subQ18,subQ17,subQ5,subQ3,subQ2])],"isStart":false}),makeQuery(id+"F27.opExtrude","SWEPT_EDGE",EDGE,{"disambiguationData":[OSD([subQ8,subQ18,subQ17,subQ5,subQ3,subQ2,subQ1])]})]}),makeQuery(id+"F28.opExtrude","SWEPT_EDGE",EDGE,{"disambiguationData":[OSD([subQ8,subQ18,subQ17,subQ5,subQ3,subQ2,sQuery(id+"F25.wireOp",EDGE,"E11")])]})]});var subQ20=makeQuery(id+"F31.imprint","INTERSECT",VERTEX,{"disambiguationData":[OD(1.0)],"derivedFrom":[subQ19,subQ0]});Q0=makeQuery(id+"F31.imprint","IMPRINT",FACE,{"disambiguationData":[TD([[makeQuery(id+"F31.imprint","IMPRINT",EDGE,{"disambiguationData":[TD([[subQ20,1.0]])],"derivedFrom":subQ0}),-1.0]])]});}
            extrude(context, id + "F32", {"entities" : qUnion([Q0]), "operationType" : NewBodyOperationType.REMOVE, "oppositeDirection" : true, "depth" : 25.4 * mm, "offsetDistance" : 25.4 * mm});
        }
        {
            var Q0;
            {var subQ0=sQuery(id+"F8.wireOp",EDGE,"E6.left");var subQ1=sQuery(id+"F8.wireOp",EDGE,"E6.bottom");var subQ2=sQuery(id+"F6.wireOp",EDGE,"E4");var subQ3=sQuery(id+"F0.wireOp",EDGE,"E0.right");var subQ4=sQuery(id+"F0.wireOp",EDGE,"E0.bottom");var subQ5=sQuery(id+"F23.wireOp",EDGE,"E9");var subQ6=sQuery(id+"F8.wireOp",EDGE,"E6.right");var subQ7=sQuery(id+"F8.wireOp",EDGE,"E6.top");var subQ8=sQuery(id+"F6.wireOp",EDGE,"E5");var subQ9=sQuery(id+"F0.wireOp",EDGE,"E0.left");var subQ10=makeQuery(id+"F24.opExtrude","CAP_EDGE",EDGE,{"disambiguationData":[OSD([subQ4,subQ9,subQ8,subQ1,subQ7,subQ0,subQ6,subQ5])],"isStart":true});var subQ11=makeQuery(id+"F9.opExtrude","SWEPT_FACE",FACE,{"disambiguationData":[OSD([subQ1])]});var subQ15=makeQuery(id+"F10.opExtrude","SWEPT_FACE",FACE,{"disambiguationData":[OSD([subQ1])]});var subQ16=makeQuery(id+"F3.boolean.opBoolean","MERGE",EDGE,{"derivedFrom":[makeQuery(id+"F2.boolean.opBoolean","MERGE",EDGE,{"derivedFrom":[makeQuery(id+"F1.opExtrude","SWEPT_EDGE",EDGE,{"disambiguationData":[OSD([subQ4,subQ9])]}),makeQuery(id+"F2.opExtrude","SWEPT_EDGE",EDGE,{"disambiguationData":[OSD([subQ4,subQ9])]})]}),makeQuery(id+"F3.opExtrude","SWEPT_EDGE",EDGE,{"disambiguationData":[OSD([subQ4,subQ9])]})]});var subQ17=makeQuery(id+"F7.boolean.opBoolean","SPLIT",EDGE,{"derivedFrom":subQ16});Q0=makeQuery(id+"F28.boolean.opBoolean","MERGE",FACE,{"derivedFrom":[makeQuery(id+"F27.boolean.opBoolean","MERGE",FACE,{"derivedFrom":[makeQuery(id+"F22.boolean.opBoolean","MERGE",FACE,{"derivedFrom":[makeQuery(id+"F15.boolean.opBoolean","MERGE",FACE,{"derivedFrom":[makeQuery(id+"F13.opExtrude","SWEPT_FACE",FACE,{"disambiguationData":[OSD([subQ4,subQ3,subQ2,subQ1,subQ0])]}),makeQuery(id+"F15.opExtrude","SWEPT_FACE",FACE,{"disambiguationData":[OSD([subQ4,subQ3,subQ2,subQ1,subQ0])]})]}),makeQuery(id+"F15.boolean.opBoolean","MERGE",FACE,{"derivedFrom":[makeQuery(id+"F14.boolean.opBoolean","MERGE",FACE,{"derivedFrom":[makeQuery(id+"F10.boolean.opBoolean","MERGE",FACE,{"derivedFrom":[subQ11,subQ15]}),makeQuery(id+"F14.opExtrude","SWEPT_FACE",FACE,{"disambiguationData":[OSD([subQ1,subQ6])]})]}),makeQuery(id+"F15.opExtrude","SWEPT_FACE",FACE,{"disambiguationData":[OSD([subQ1,subQ6])]})]}),makeQuery(id+"F22.opExtrude","SWEPT_FACE",FACE,{"disambiguationData":[OSD([subQ4,subQ3,subQ2,subQ1,subQ0,subQ6])]})]}),makeQuery(id+"F27.opExtrude","SWEPT_FACE",FACE,{"disambiguationData":[OSD([subQ4,subQ9,subQ8,subQ1,subQ7,subQ0,subQ6,subQ5]),TDD([makeQuery(id+"F24.boolean.opBoolean","MERGE",EDGE,{"derivedFrom":[makeQuery(id+"F22.boolean.opBoolean","MERGE",EDGE,{"derivedFrom":[makeQuery(id+"F12.boolean.opBoolean","MERGE",EDGE,{"derivedFrom":[makeQuery(id+"F10.boolean.opBoolean","SPLIT",EDGE,{"disambiguationData":[topologyDisambiguationEdgeConnected([makeQuery(id+"F1.opExtrude","SWEPT_FACE",FACE,{"disambiguationData":[OSD([subQ4])]})])],"derivedFrom":subQ17}),makeQuery(id+"F12.opExtrude","SWEPT_EDGE",EDGE,{"disambiguationData":[OSD([subQ4,subQ9,subQ8,subQ1,subQ7,subQ0,subQ6])]})]}),makeQuery(id+"F15.boolean.opBoolean","MERGE",EDGE,{"derivedFrom":[makeQuery(id+"F11.boolean.opBoolean","MERGE",EDGE,{"derivedFrom":[makeQuery(id+"F7.boolean.opBoolean","MERGE",EDGE,{"derivedFrom":[subQ16,makeQuery(id+"F7.opExtrude","SWEPT_EDGE",EDGE,{"disambiguationData":[OSD([subQ4,subQ9,subQ8])]})]}),makeQuery(id+"F10.boolean.opBoolean","SPLIT",EDGE,{"disambiguationData":[topologyDisambiguationEdgeConnected([subQ11])],"derivedFrom":subQ17}),makeQuery(id+"F11.opExtrude","SWEPT_EDGE",EDGE,{"disambiguationData":[OSD([subQ4,subQ9,subQ8])]})]}),makeQuery(id+"F15.opExtrude","SWEPT_EDGE",EDGE,{"disambiguationData":[OSD([subQ4,subQ9,subQ8])]})]})]}),subQ10]}),makeQuery(id+"F24.boolean.opBoolean","COPY",EDGE,{"derivedFrom":subQ10})])]})]}),makeQuery(id+"F28.opExtrude","SWEPT_FACE",FACE,{"disambiguationData":[OSD([subQ4,subQ3,subQ2,subQ1,subQ0,sQuery(id+"F25.wireOp",EDGE,"E11")])]})]});}
            var sketch = newSketch(context, id + "F33", { "sketchPlane" : qUnion([Q0])});
            skArc(sketch, "E17", {"start": v(20.83, -83.82) * mm, "mid": v(28.32, -81.73) * mm, "end": v(31.14, -74.47) * mm});
            skSolve(sketch);
        }
        {
            var Q0;
            {var subQ0=sQuery(id+"F33.wireOp",EDGE,"E17");var subQ1=sQuery(id+"F25.wireOp",EDGE,"E11");var subQ3=sQuery(id+"F8.wireOp",EDGE,"E6.left");var subQ4=sQuery(id+"F8.wireOp",EDGE,"E6.bottom");var subQ5=sQuery(id+"F6.wireOp",EDGE,"E4");var subQ6=sQuery(id+"F0.wireOp",EDGE,"E0.right");var subQ7=sQuery(id+"F0.wireOp",EDGE,"E0.bottom");var subQ10=makeQuery(id+"F28.opExtrude","CAP_EDGE",EDGE,{"disambiguationData":[OSD([subQ7,subQ6,subQ5,subQ4,subQ3,subQ1])],"isStart":false});var subQ11=makeQuery(id+"F33.imprint","INTERSECT",VERTEX,{"disambiguationData":[OD(1.0)],"derivedFrom":[subQ10,subQ0]});Q0=makeQuery(id+"F33.imprint","IMPRINT",FACE,{"disambiguationData":[TD([[makeQuery(id+"F33.imprint","IMPRINT",EDGE,{"disambiguationData":[TD([[subQ11,1.0]])],"derivedFrom":subQ0}),-1.0]])]});}
            extrude(context, id + "F34", {"entities" : qUnion([Q0]), "operationType" : NewBodyOperationType.REMOVE, "oppositeDirection" : true, "depth" : 25.4 * mm, "offsetDistance" : 25.4 * mm});
        }
        {
            var Q0;
            {var subQ0=sQuery(id+"F8.wireOp",EDGE,"E6.left");var subQ1=sQuery(id+"F8.wireOp",EDGE,"E6.bottom");var subQ2=sQuery(id+"F6.wireOp",EDGE,"E4");var subQ3=sQuery(id+"F0.wireOp",EDGE,"E0.right");var subQ4=sQuery(id+"F0.wireOp",EDGE,"E0.bottom");var subQ5=sQuery(id+"F23.wireOp",EDGE,"E9");var subQ6=sQuery(id+"F8.wireOp",EDGE,"E6.right");var subQ7=sQuery(id+"F8.wireOp",EDGE,"E6.top");var subQ8=sQuery(id+"F6.wireOp",EDGE,"E5");var subQ9=sQuery(id+"F0.wireOp",EDGE,"E0.left");var subQ10=makeQuery(id+"F24.opExtrude","CAP_EDGE",EDGE,{"disambiguationData":[OSD([subQ4,subQ9,subQ8,subQ1,subQ7,subQ0,subQ6,subQ5])],"isStart":true});var subQ11=makeQuery(id+"F9.opExtrude","SWEPT_FACE",FACE,{"disambiguationData":[OSD([subQ1])]});var subQ15=makeQuery(id+"F10.opExtrude","SWEPT_FACE",FACE,{"disambiguationData":[OSD([subQ1])]});var subQ16=makeQuery(id+"F3.boolean.opBoolean","MERGE",EDGE,{"derivedFrom":[makeQuery(id+"F2.boolean.opBoolean","MERGE",EDGE,{"derivedFrom":[makeQuery(id+"F1.opExtrude","SWEPT_EDGE",EDGE,{"disambiguationData":[OSD([subQ4,subQ9])]}),makeQuery(id+"F2.opExtrude","SWEPT_EDGE",EDGE,{"disambiguationData":[OSD([subQ4,subQ9])]})]}),makeQuery(id+"F3.opExtrude","SWEPT_EDGE",EDGE,{"disambiguationData":[OSD([subQ4,subQ9])]})]});var subQ17=makeQuery(id+"F7.boolean.opBoolean","SPLIT",EDGE,{"derivedFrom":subQ16});Q0=makeQuery(id+"F28.boolean.opBoolean","MERGE",FACE,{"derivedFrom":[makeQuery(id+"F27.boolean.opBoolean","MERGE",FACE,{"derivedFrom":[makeQuery(id+"F22.boolean.opBoolean","MERGE",FACE,{"derivedFrom":[makeQuery(id+"F15.boolean.opBoolean","MERGE",FACE,{"derivedFrom":[makeQuery(id+"F13.opExtrude","SWEPT_FACE",FACE,{"disambiguationData":[OSD([subQ4,subQ3,subQ2,subQ1,subQ0])]}),makeQuery(id+"F15.opExtrude","SWEPT_FACE",FACE,{"disambiguationData":[OSD([subQ4,subQ3,subQ2,subQ1,subQ0])]})]}),makeQuery(id+"F15.boolean.opBoolean","MERGE",FACE,{"derivedFrom":[makeQuery(id+"F14.boolean.opBoolean","MERGE",FACE,{"derivedFrom":[makeQuery(id+"F10.boolean.opBoolean","MERGE",FACE,{"derivedFrom":[subQ11,subQ15]}),makeQuery(id+"F14.opExtrude","SWEPT_FACE",FACE,{"disambiguationData":[OSD([subQ1,subQ6])]})]}),makeQuery(id+"F15.opExtrude","SWEPT_FACE",FACE,{"disambiguationData":[OSD([subQ1,subQ6])]})]}),makeQuery(id+"F22.opExtrude","SWEPT_FACE",FACE,{"disambiguationData":[OSD([subQ4,subQ3,subQ2,subQ1,subQ0,subQ6])]})]}),makeQuery(id+"F27.opExtrude","SWEPT_FACE",FACE,{"disambiguationData":[OSD([subQ4,subQ9,subQ8,subQ1,subQ7,subQ0,subQ6,subQ5]),TDD([makeQuery(id+"F24.boolean.opBoolean","MERGE",EDGE,{"derivedFrom":[makeQuery(id+"F22.boolean.opBoolean","MERGE",EDGE,{"derivedFrom":[makeQuery(id+"F12.boolean.opBoolean","MERGE",EDGE,{"derivedFrom":[makeQuery(id+"F10.boolean.opBoolean","SPLIT",EDGE,{"disambiguationData":[topologyDisambiguationEdgeConnected([makeQuery(id+"F1.opExtrude","SWEPT_FACE",FACE,{"disambiguationData":[OSD([subQ4])]})])],"derivedFrom":subQ17}),makeQuery(id+"F12.opExtrude","SWEPT_EDGE",EDGE,{"disambiguationData":[OSD([subQ4,subQ9,subQ8,subQ1,subQ7,subQ0,subQ6])]})]}),makeQuery(id+"F15.boolean.opBoolean","MERGE",EDGE,{"derivedFrom":[makeQuery(id+"F11.boolean.opBoolean","MERGE",EDGE,{"derivedFrom":[makeQuery(id+"F7.boolean.opBoolean","MERGE",EDGE,{"derivedFrom":[subQ16,makeQuery(id+"F7.opExtrude","SWEPT_EDGE",EDGE,{"disambiguationData":[OSD([subQ4,subQ9,subQ8])]})]}),makeQuery(id+"F10.boolean.opBoolean","SPLIT",EDGE,{"disambiguationData":[topologyDisambiguationEdgeConnected([subQ11])],"derivedFrom":subQ17}),makeQuery(id+"F11.opExtrude","SWEPT_EDGE",EDGE,{"disambiguationData":[OSD([subQ4,subQ9,subQ8])]})]}),makeQuery(id+"F15.opExtrude","SWEPT_EDGE",EDGE,{"disambiguationData":[OSD([subQ4,subQ9,subQ8])]})]})]}),subQ10]}),makeQuery(id+"F24.boolean.opBoolean","COPY",EDGE,{"derivedFrom":subQ10})])]})]}),makeQuery(id+"F28.opExtrude","SWEPT_FACE",FACE,{"disambiguationData":[OSD([subQ4,subQ3,subQ2,subQ1,subQ0,sQuery(id+"F25.wireOp",EDGE,"E11")])]})]});}
            var sketch = newSketch(context, id + "F35", { "sketchPlane" : qUnion([Q0])});
            skCircle(sketch, "E18", {"center": v(16.8, -72.28) * mm, "radius": 6.1 * mm});
            skSolve(sketch);
        }
        {
            var Q0;
            Q0=makeQuery(id+"F35.imprint","IMPRINT",FACE,{"disambiguationData":[TD([[makeQuery(id+"F35.imprint","IMPRINT",EDGE,{"derivedFrom":sQuery(id+"F35.wireOp",EDGE,"E18")}),1.0]])]});
            extrude(context, id + "F36", {"entities" : qUnion([Q0]), "operationType" : NewBodyOperationType.REMOVE, "oppositeDirection" : true, "depth" : 25.4 * mm, "offsetDistance" : 25.4 * mm});
        }
        {
            var Q0;
            Q0=makeQuery(id+"F20.opExtrude","CAP_FACE",FACE,{"disambiguationData":[OSD([sQuery(id+"F19.wireOp",EDGE,"E8")])],"isStart":false});
            var sketch = newSketch(context, id + "F37", { "sketchPlane" : qUnion([Q0])});
            skCircle(sketch, "E19", {"center": v(-31.17, 57.22) * mm, "radius": 9.12 * mm});
            skSolve(sketch);
        }
        {
            var Q0;
            Q0=makeQuery(id+"F37.imprint","IMPRINT",FACE,{"disambiguationData":[TD([[makeQuery(id+"F37.imprint","IMPRINT",EDGE,{"derivedFrom":sQuery(id+"F37.wireOp",EDGE,"E19")}),1.0]])]});
            extrude(context, id + "F38", {"entities" : qUnion([Q0]), "operationType" : NewBodyOperationType.REMOVE, "oppositeDirection" : true, "depth" : 25.4 * mm, "offsetDistance" : 25.4 * mm});
        }
    });
